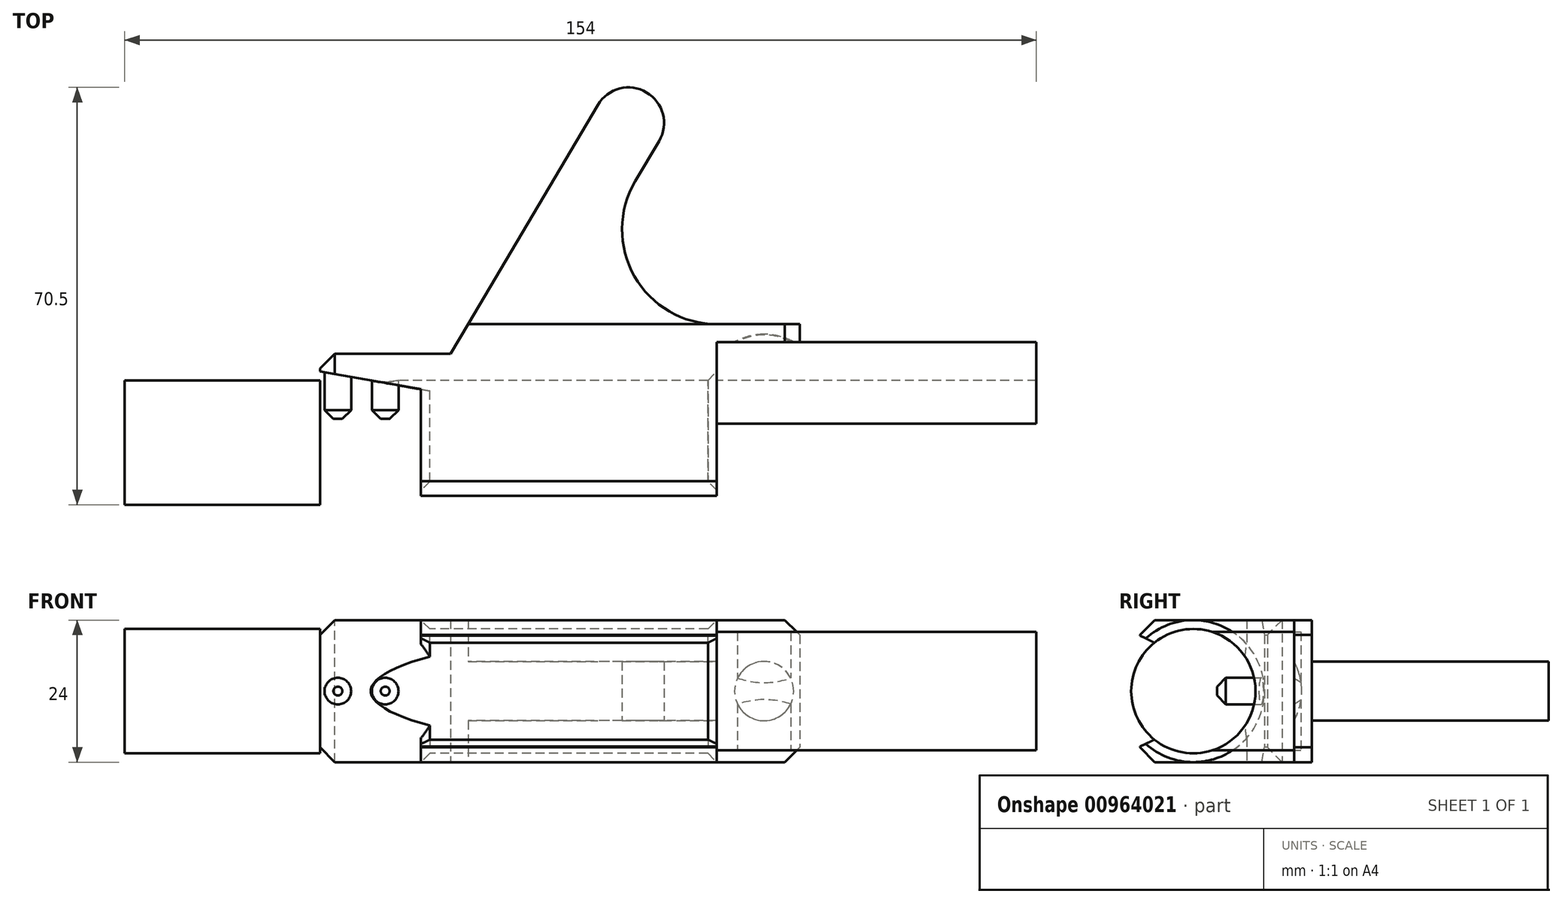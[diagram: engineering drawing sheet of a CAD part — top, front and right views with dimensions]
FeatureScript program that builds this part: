
annotation { "Feature Type Name" : "Feature", "Feature Type Description" : "" }
export const myFeature = defineFeature(function(context is Context, id is Id, definition is map)
    precondition{}
    {
        {
            var Q0;
            Q0=qCreatedBy(makeId("Right.planeOp"),FACE);
            var sketch = newSketch(context, id + "F0", { "sketchPlane" : qUnion([Q0])});
            skCircle(sketch, "E0", {"center": v(0, 0) * mm, "radius": 10.5 * mm});
            skSolve(sketch);
        }
        {
            var Q0;
            Q0=qSketchRegion(id+"F0",true);
            extrude(context, id + "F1", {"entities" : qUnion([Q0]), "depth" : 200 * mm, "offsetDistance" : 25 * mm, "symmetric" : true});
        }
        {
            var Q0;
            Q0=qCreatedBy(makeId("Front.planeOp"),FACE);
            var sketch = newSketch(context, id + "F2", { "sketchPlane" : qUnion([Q0])});
            skCircle(sketch, "E1", {"center": v(8, 0) * mm, "radius": 2.5 * mm});
            skCircle(sketch, "E2", {"center": v(-64, 0) * mm, "radius": 2.5 * mm});
            skCircle(sketch, "E3", {"center": v(-56, 0) * mm, "radius": 2.5 * mm});
            skSolve(sketch);
        }
        {
            var Q0;
            Q0=qSketchRegion(id+"F2",true);
            extrude(context, id + "F3", {"entities" : qUnion([Q0]), "operationType" : NewBodyOperationType.REMOVE, "endBound" : BoundingType.THROUGH_ALL, "oppositeDirection" : true, "depth" : 25 * mm, "offsetDistance" : 25 * mm});
        }
        {
            var Q0;
            Q0=qCreatedBy(makeId("Top.planeOp"),FACE);
            var sketch = newSketch(context, id + "F4", { "sketchPlane" : qUnion([Q0])});
            skLineSegment(sketch, "E4.bottom", {"start": v(0, 17) * mm, "end": v(54, 17) * mm});
            skLineSegment(sketch, "E4.top", {"start": v(0, 0) * mm, "end": v(54, 0) * mm});
            skLineSegment(sketch, "E4.left", {"start": v(0, 17) * mm, "end": v(0, 0) * mm});
            skLineSegment(sketch, "E4.right", {"start": v(54, 17) * mm, "end": v(54, 0) * mm});
            skArc(sketch, "E5", {"start": v(12.5, 17) * mm, "mid": v(8, 18.2) * mm, "end": v(3.5, 17) * mm});
            skSolve(sketch);
        }
        {
            var Q0;
            Q0=qSketchRegion(id+"F4",true);
            extrude(context, id + "F5", {"entities" : qUnion([Q0]), "depth" : 20 * mm, "offsetDistance" : 25 * mm, "symmetric" : true});
        }
        {
            var Q0;
            Q0=qCreatedBy(makeId("Top.planeOp"),FACE);
            var sketch = newSketch(context, id + "F6", { "sketchPlane" : qUnion([Q0])});
            skLineSegment(sketch, "E6.bottom", {"start": v(14, 20) * mm, "end": v(-42, 20) * mm});
            skLineSegment(sketch, "E6.top", {"start": v(0, -9) * mm, "end": v(-49.96, -9) * mm});
            skLineSegment(sketch, "E6.left", {"start": v(0, 17) * mm, "end": v(0, -9) * mm});
            skLineSegment(sketch, "E6.right", {"start": v(-49.96, 9) * mm, "end": v(-49.96, -9) * mm});
            skLineSegment(sketch, "E7.top", {"start": v(14, 17) * mm, "end": v(0, 17) * mm});
            skLineSegment(sketch, "E7.left", {"start": v(14, 20) * mm, "end": v(14, 17) * mm});
            skLineSegment(sketch, "E8", {"start": v(-67, 15) * mm, "end": v(-67, 12) * mm});
            skLineSegment(sketch, "E9", {"start": v(-67, 12) * mm, "end": v(-49.96, 9) * mm});
            skLineSegment(sketch, "E10", {"start": v(-42, 20) * mm, "end": v(-20.08, 57.06) * mm});
            skArc(sketch, "E11", {"start": v(-13.77, 44.15) * mm, "mid": v(-13.9, 28.07) * mm, "end": v(0, 20) * mm});
            skArc(sketch, "E12", {"start": v(-9.75, 50.94) * mm, "mid": v(-11.86, 59.16) * mm, "end": v(-20.08, 57.06) * mm});
            skLineSegment(sketch, "E13", {"start": v(-20.08, 57.06) * mm, "end": v(-9.75, 50.94) * mm, "construction": true});
            skLineSegment(sketch, "E14", {"start": v(-9.75, 50.94) * mm, "end": v(-13.77, 44.15) * mm});
            skLineSegment(sketch, "E15", {"start": v(-67, 15) * mm, "end": v(-44.96, 15) * mm});
            skLineSegment(sketch, "E16", {"start": v(-44.96, 15) * mm, "end": v(-42, 20) * mm});
            skArc(sketch, "E17", {"start": v(13, 17) * mm, "mid": v(8, 18.3) * mm, "end": v(3, 17) * mm});
            skLineSegment(sketch, "E18", {"start": v(8, 17) * mm, "end": v(8, 18.3) * mm});
            skSolve(sketch);
        }
        {
            var Q0;
            Q0=makeQuery(id+"F6.imprint","IMPRINT",FACE,{"disambiguationData":[TD([[makeQuery(id+"F6.imprint","IMPRINT",EDGE,{"derivedFrom":sQuery(id+"F6.wireOp",EDGE,"E6.top")}),-1.0]])]});
            var Q1;
            {var subQ3=sQuery(id+"F6.wireOp",EDGE,"E18");Q1=makeQuery(id+"F6.imprint","IMPRINT",FACE,{"disambiguationData":[TD([[makeQuery(id+"F6.imprint","IMPRINT",EDGE,{"derivedFrom":subQ3}),1.0]])]});}
            var Q2;
            {var subQ3=sQuery(id+"F6.wireOp",EDGE,"E18");Q2=makeQuery(id+"F6.imprint","IMPRINT",FACE,{"disambiguationData":[TD([[makeQuery(id+"F6.imprint","IMPRINT",EDGE,{"derivedFrom":subQ3}),-1.0]])]});}
            extrude(context, id + "F7", {"entities" : qUnion([Q0, Q1, Q2]), "depth" : 24 * mm, "offsetDistance" : 25 * mm, "symmetric" : true});
        }
        {
            var Q0;
            {var subQ0=sQuery(id+"F6.wireOp",EDGE,"E10");Q0=makeQuery(id+"F6.imprint","IMPRINT",FACE,{"disambiguationData":[TD([[makeQuery(id+"F6.imprint","IMPRINT",EDGE,{"derivedFrom":subQ0}),-1.0]])]});}
            extrude(context, id + "F8", {"entities" : qUnion([Q0]), "operationType" : NewBodyOperationType.ADD, "depth" : 10 * mm, "offsetDistance" : 25 * mm, "symmetric" : true});
        }
        {
            var Q0;
            Q0=makeQuery(id+"F7.opExtrude","SWEPT_FACE",FACE,{"disambiguationData":[OSD([sQuery(id+"F6.wireOp",EDGE,"E8")])]});
            var sketch = newSketch(context, id + "F9", { "sketchPlane" : qUnion([Q0])});
            skCircle(sketch, "E19", {"center": v(0, 0) * mm, "radius": 10.5 * mm});
            skSolve(sketch);
        }
        {
            var Q0;
            Q0=qSketchRegion(id+"F9",true);
            extrude(context, id + "F10", {"entities" : qUnion([Q0]), "operationType" : NewBodyOperationType.REMOVE, "endBound" : BoundingType.THROUGH_ALL, "oppositeDirection" : true, "depth" : 25 * mm, "offsetDistance" : 25 * mm});
        }
        {
            var Q0;
            Q0=makeQuery(id+"F7.opExtrude","SWEPT_FACE",FACE,{"disambiguationData":[OSD([sQuery(id+"F6.wireOp",EDGE,"E15")])]});
            var sketch = newSketch(context, id + "F11", { "sketchPlane" : qUnion([Q0])});
            skCircle(sketch, "E20", {"center": v(64, 0) * mm, "radius": 2.25 * mm});
            skCircle(sketch, "E21", {"center": v(56, 0) * mm, "radius": 2.25 * mm});
            skSolve(sketch);
        }
        {
            var Q0;
            Q0=qSketchRegion(id+"F11",true);
            extrude(context, id + "F12", {"entities" : qUnion([Q0]), "operationType" : NewBodyOperationType.ADD, "oppositeDirection" : true, "depth" : 11 * mm, "offsetDistance" : 2 * mm});
        }
        {
            var Q0;
            {var subQ3=sQuery(id+"F6.wireOp",EDGE,"E18");Q0=makeQuery(id+"F6.imprint","IMPRINT",FACE,{"disambiguationData":[TD([[makeQuery(id+"F6.imprint","IMPRINT",EDGE,{"derivedFrom":subQ3}),-1.0]])]});}
            var Q1;
            Q1=sQuery(id+"F6.wireOp",EDGE,"E18");
            revolve(context, id + "F13", {"operationType" : NewBodyOperationType.REMOVE, "surfaceOperationType" : NewSurfaceOperationType.NEW, "entities" : qUnion([Q0]), "axis" : qUnion([Q1]), "revolveType" : RevolveType.FULL, "oppositeDirection" : true});
        }
        {
            var Q0;
            Q0=makeQuery(id+"F10.boolean.opBoolean","INTERSECT",EDGE,{"disambiguationData":[OD(0.0)],"derivedFrom":[makeQuery(id+"F7.opExtrude","SWEPT_FACE",FACE,{"disambiguationData":[OSD([sQuery(id+"F6.wireOp",EDGE,"E6.top")])]}),makeQuery(id+"F10.opExtrude","SWEPT_FACE",FACE,{"disambiguationData":[OSD([sQuery(id+"F9.wireOp",EDGE,"E19")])]})]});
            var Q1;
            Q1=makeQuery(id+"F10.boolean.opBoolean","INTERSECT",EDGE,{"disambiguationData":[OD(1.0)],"derivedFrom":[makeQuery(id+"F7.opExtrude","SWEPT_FACE",FACE,{"disambiguationData":[OSD([sQuery(id+"F6.wireOp",EDGE,"E6.top")])]}),makeQuery(id+"F10.opExtrude","SWEPT_FACE",FACE,{"disambiguationData":[OSD([sQuery(id+"F9.wireOp",EDGE,"E19")])]})]});
            var Q2;
            Q2=makeQuery(id+"F12.opExtrude","CAP_FACE",FACE,{"disambiguationData":[OSD([sQuery(id+"F2.wireOp",EDGE,"E2")])],"isStart":true});
            var Q3;
            Q3=makeQuery(id+"F10.boolean.opBoolean","INTERSECT",EDGE,{"derivedFrom":[makeQuery(id+"F7.opExtrude","SWEPT_FACE",FACE,{"disambiguationData":[OSD([sQuery(id+"F6.wireOp",EDGE,"E6.left")])]}),makeQuery(id+"F10.opExtrude","SWEPT_FACE",FACE,{"disambiguationData":[OSD([sQuery(id+"F9.wireOp",EDGE,"E19")])]})]});
            var Q4;
            Q4=makeQuery(id+"F10.boolean.opBoolean","INTERSECT",EDGE,{"disambiguationData":[OD(0.0)],"derivedFrom":[makeQuery(id+"F7.opExtrude","SWEPT_FACE",FACE,{"disambiguationData":[OSD([sQuery(id+"F6.wireOp",EDGE,"E6.right")])]}),makeQuery(id+"F10.opExtrude","SWEPT_FACE",FACE,{"disambiguationData":[OSD([sQuery(id+"F9.wireOp",EDGE,"E19")])]})]});
            var Q5;
            Q5=makeQuery(id+"F10.boolean.opBoolean","INTERSECT",EDGE,{"disambiguationData":[OD(1.0)],"derivedFrom":[makeQuery(id+"F7.opExtrude","SWEPT_FACE",FACE,{"disambiguationData":[OSD([sQuery(id+"F6.wireOp",EDGE,"E6.right")])]}),makeQuery(id+"F10.opExtrude","SWEPT_FACE",FACE,{"disambiguationData":[OSD([sQuery(id+"F9.wireOp",EDGE,"E19")])]})]});
            var Q6;
            Q6=makeQuery(id+"F12.opExtrude","CAP_EDGE",EDGE,{"disambiguationData":[OSD([sQuery(id+"F11.wireOp",EDGE,"E20")])],"isStart":false});
            var Q7;
            Q7=makeQuery(id+"F12.opExtrude","CAP_EDGE",EDGE,{"disambiguationData":[OSD([sQuery(id+"F11.wireOp",EDGE,"E21")])],"isStart":false});
            chamfer(context, id + "F14", {"entities" : qUnion([Q0, Q1, Q2, Q3, Q4, Q5, Q6, Q7]), "width" : 1.5 * mm, "tangentPropagation" : true});
        }
        {
            var Q0;
            Q0=makeQuery(id+"F7.opExtrude","CAP_EDGE",EDGE,{"disambiguationData":[OSD([sQuery(id+"F6.wireOp",EDGE,"E6.top")])],"isStart":true});
            var Q1;
            Q1=makeQuery(id+"F7.opExtrude","CAP_EDGE",EDGE,{"disambiguationData":[OSD([sQuery(id+"F6.wireOp",EDGE,"E6.top")])],"isStart":false});
            var Q2;
            Q2=makeQuery(id+"F8.opExtrude","CAP_EDGE",EDGE,{"disambiguationData":[OSD([sQuery(id+"F6.wireOp",EDGE,"E6.bottom")])],"isStart":true});
            var Q3;
            Q3=makeQuery(id+"F8.opExtrude","CAP_EDGE",EDGE,{"disambiguationData":[OSD([sQuery(id+"F6.wireOp",EDGE,"E6.bottom")])],"isStart":false});
            var Q4;
            Q4=makeQuery(id+"F12.boolean.opBoolean","INTERSECT",EDGE,{"derivedFrom":[makeQuery(id+"F7.opExtrude","SWEPT_FACE",FACE,{"disambiguationData":[OSD([sQuery(id+"F6.wireOp",EDGE,"E15")])]}),makeQuery(id+"F12.opExtrude","SWEPT_FACE",FACE,{"disambiguationData":[OSD([sQuery(id+"F2.wireOp",EDGE,"E2")])]})]});
            var Q5;
            Q5=makeQuery(id+"F7.opExtrude","CAP_EDGE",EDGE,{"disambiguationData":[OSD([sQuery(id+"F6.wireOp",EDGE,"E8")])],"isStart":true});
            var Q6;
            Q6=makeQuery(id+"F7.opExtrude","CAP_EDGE",EDGE,{"disambiguationData":[OSD([sQuery(id+"F6.wireOp",EDGE,"E8")])],"isStart":false});
            var Q7;
            Q7=makeQuery(id+"F7.opExtrude","CAP_EDGE",EDGE,{"disambiguationData":[OSD([sQuery(id+"F6.wireOp",EDGE,"E7.left")])],"isStart":true});
            var Q8;
            Q8=makeQuery(id+"F7.opExtrude","CAP_EDGE",EDGE,{"disambiguationData":[OSD([sQuery(id+"F6.wireOp",EDGE,"E7.left")])],"isStart":false});
            var Q9;
            Q9=makeQuery(id+"F7.opExtrude","SWEPT_EDGE",EDGE,{"disambiguationData":[OSD([sQuery(id+"F6.wireOp",EDGE,"E8"),sQuery(id+"F6.wireOp",EDGE,"E15")])]});
            chamfer(context, id + "F15", {"entities" : qUnion([Q0, Q1, Q2, Q3, Q4, Q5, Q6, Q7, Q8, Q9]), "width" : 2.5 * mm, "tangentPropagation" : true});
        }
    });
